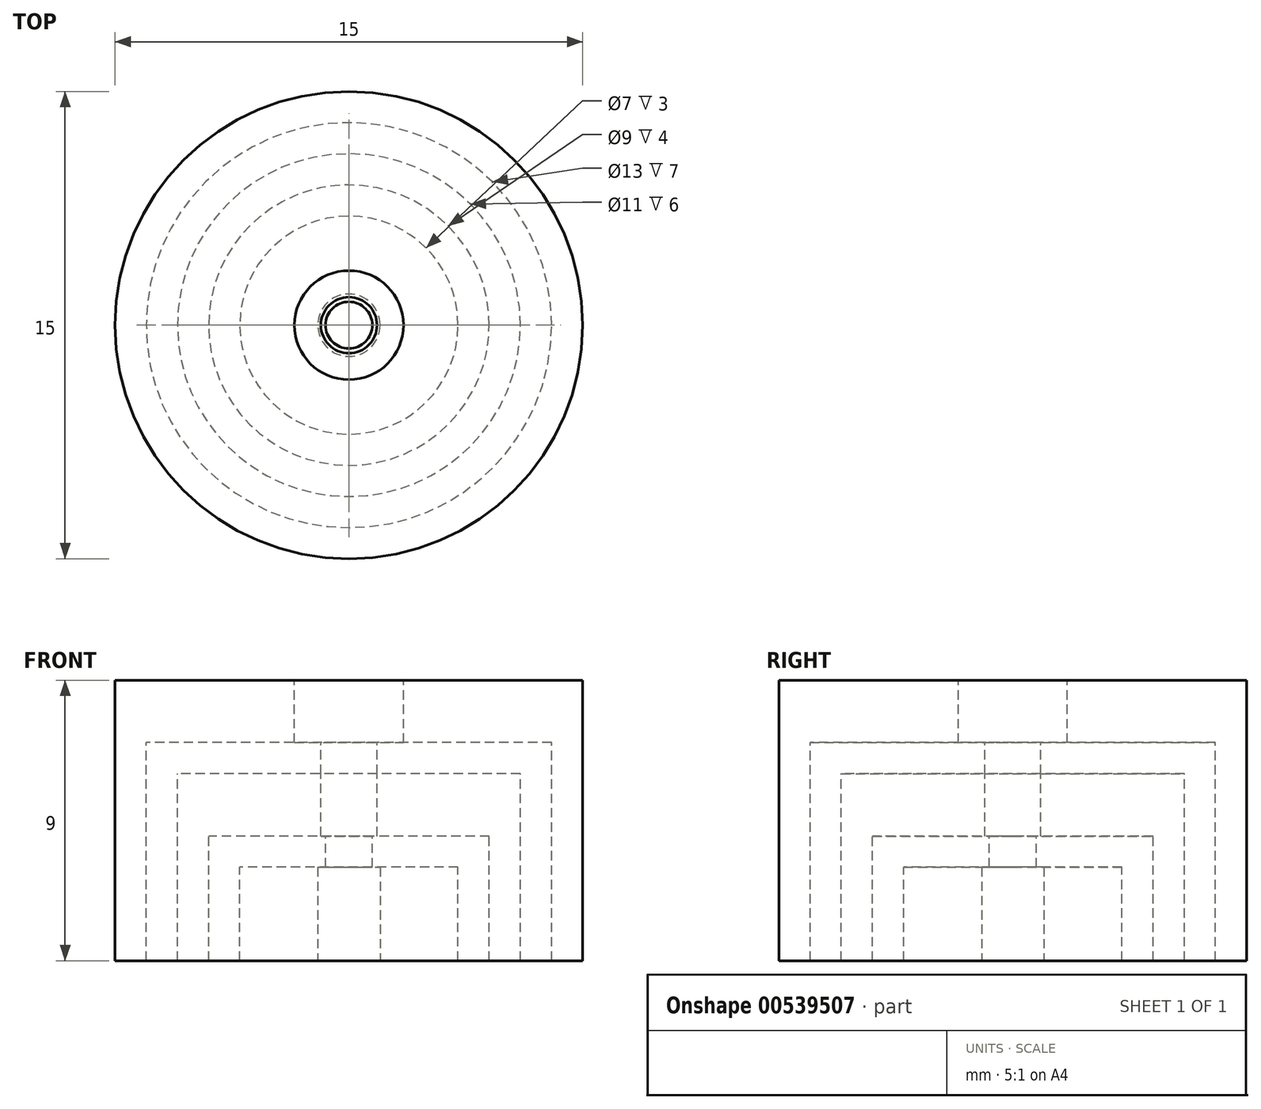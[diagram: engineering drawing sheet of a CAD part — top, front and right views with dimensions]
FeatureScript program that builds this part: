
annotation { "Feature Type Name" : "Feature", "Feature Type Description" : "" }
export const myFeature = defineFeature(function(context is Context, id is Id, definition is map)
    precondition{}
    {
        {
            var Q0;
            Q0=qCreatedBy(makeId("Front.planeOp"),FACE);
            var sketch = newSketch(context, id + "F0", { "sketchPlane" : qUnion([Q0])});
            skLineSegment(sketch, "E0", {"start": v(0, 0) * mm, "end": v(3.5, 0) * mm});
            skLineSegment(sketch, "E1", {"start": v(3.5, 0) * mm, "end": v(3.5, 3) * mm});
            skLineSegment(sketch, "E2", {"start": v(3.5, 3) * mm, "end": v(0, 3) * mm});
            skLineSegment(sketch, "E3", {"start": v(0, 3) * mm, "end": v(0, 0) * mm});
            skLineSegment(sketch, "E4", {"start": v(3.5, 0) * mm, "end": v(4.5, 0) * mm});
            skLineSegment(sketch, "E5", {"start": v(4.5, 0) * mm, "end": v(4.5, 4) * mm});
            skLineSegment(sketch, "E6", {"start": v(4.5, 4) * mm, "end": v(0, 4) * mm});
            skLineSegment(sketch, "E7", {"start": v(0, 5.5) * mm, "end": v(0, 0) * mm});
            skLineSegment(sketch, "E8", {"start": v(4.5, 0) * mm, "end": v(5.5, 0) * mm});
            skLineSegment(sketch, "E9", {"start": v(5.5, 0) * mm, "end": v(5.5, 6) * mm});
            skLineSegment(sketch, "E10", {"start": v(5.5, 6) * mm, "end": v(0, 6) * mm});
            skLineSegment(sketch, "E11", {"start": v(0, 9) * mm, "end": v(0, 0) * mm});
            skLineSegment(sketch, "E12", {"start": v(5.5, 0) * mm, "end": v(6.5, 0) * mm});
            skLineSegment(sketch, "E13", {"start": v(6.5, 0) * mm, "end": v(6.5, 7) * mm});
            skLineSegment(sketch, "E14", {"start": v(6.5, 7) * mm, "end": v(0, 7) * mm});
            skLineSegment(sketch, "E15", {"start": v(6.5, 0) * mm, "end": v(7.5, 0) * mm});
            skLineSegment(sketch, "E16", {"start": v(7.5, 0) * mm, "end": v(7.5, 9) * mm});
            skLineSegment(sketch, "E17", {"start": v(7.5, 9) * mm, "end": v(0, 9) * mm});
            skSolve(sketch);
        }
        {
            var Q0;
            Q0=makeQuery(id+"F0.imprint","IMPRINT",FACE,{"disambiguationData":[TD([[makeQuery(id+"F0.imprint","IMPRINT",EDGE,{"derivedFrom":sQuery(id+"F0.wireOp",EDGE,"E0")}),1.0]])]});
            var Q1;
            Q1=sQuery(id+"F0.wireOp",EDGE,"E3");
            revolve(context, id + "F1", {"entities" : qUnion([Q0]), "axis" : qUnion([Q1]), "revolveType" : RevolveType.FULL});
        }
        {
            var Q0;
            Q0=makeQuery(id+"F1.opRevolve","SWEPT_FACE",FACE,{"disambiguationData":[OSD([sQuery(id+"F0.wireOp",EDGE,"E0")])]});
            var sketch = newSketch(context, id + "F2", { "sketchPlane" : qUnion([Q0])});
            skCircle(sketch, "E18", {"center": v(0, 0) * mm, "radius": 1 * mm});
            skSolve(sketch);
        }
        {
            var Q0;
            Q0=makeQuery(id+"F2.imprint","IMPRINT",FACE,{"disambiguationData":[TD([[makeQuery(id+"F2.imprint","IMPRINT",EDGE,{"derivedFrom":sQuery(id+"F2.wireOp",EDGE,"E18")}),1.0]])]});
            var Q1;
            Q1=makeQuery(id+"F1.opRevolve","SWEPT_FACE",FACE,{"disambiguationData":[OSD([sQuery(id+"F0.wireOp",EDGE,"E2")])]});
            extrude(context, id + "F3", {"entities" : qUnion([Q0]), "operationType" : NewBodyOperationType.REMOVE, "endBound" : BoundingType.UP_TO_SURFACE, "oppositeDirection" : true, "depth" : 25 * mm, "endBoundEntityFace" : qUnion([Q1]), "offsetDistance" : 25 * mm});
        }
        {
            var Q0;
            Q0=makeQuery(id+"F0.imprint","IMPRINT",FACE,{"disambiguationData":[TD([[makeQuery(id+"F0.imprint","IMPRINT",EDGE,{"derivedFrom":sQuery(id+"F0.wireOp",EDGE,"E1")}),-1.0]])]});
            var Q1;
            Q1=sQuery(id+"F0.wireOp",EDGE,"E7");
            revolve(context, id + "F4", {"entities" : qUnion([Q0]), "axis" : qUnion([Q1]), "revolveType" : RevolveType.FULL});
        }
        {
            var Q0;
            Q0=makeQuery(id+"F4.opRevolve","SWEPT_FACE",FACE,{"disambiguationData":[OSD([sQuery(id+"F0.wireOp",EDGE,"E6")])]});
            var sketch = newSketch(context, id + "F5", { "sketchPlane" : qUnion([Q0])});
            skCircle(sketch, "E19", {"center": v(0, 0) * mm, "radius": 0.75 * mm});
            skSolve(sketch);
        }
        {
            var Q0;
            Q0=makeQuery(id+"F5.imprint","IMPRINT",FACE,{"disambiguationData":[TD([[makeQuery(id+"F5.imprint","IMPRINT",EDGE,{"derivedFrom":sQuery(id+"F5.wireOp",EDGE,"E19")}),1.0]])]});
            extrude(context, id + "F6", {"entities" : qUnion([Q0]), "operationType" : NewBodyOperationType.REMOVE, "endBound" : BoundingType.UP_TO_NEXT, "oppositeDirection" : true, "depth" : 25 * mm, "offsetDistance" : 25 * mm});
        }
        {
            var Q0;
            Q0=makeQuery(id+"F0.imprint","IMPRINT",FACE,{"disambiguationData":[TD([[makeQuery(id+"F0.imprint","IMPRINT",EDGE,{"derivedFrom":sQuery(id+"F0.wireOp",EDGE,"E5")}),-1.0]])]});
            var Q1;
            Q1=sQuery(id+"F0.wireOp",EDGE,"E11");
            revolve(context, id + "F7", {"entities" : qUnion([Q0]), "axis" : qUnion([Q1]), "revolveType" : RevolveType.FULL});
        }
        {
            var Q0;
            Q0=makeQuery(id+"F7.opRevolve","SWEPT_FACE",FACE,{"disambiguationData":[OSD([sQuery(id+"F0.wireOp",EDGE,"E10")])]});
            var sketch = newSketch(context, id + "F8", { "sketchPlane" : qUnion([Q0])});
            skCircle(sketch, "E20", {"center": v(0, 0) * mm, "radius": 0.9 * mm});
            skSolve(sketch);
        }
        {
            var Q0;
            Q0=makeQuery(id+"F8.imprint","IMPRINT",FACE,{"disambiguationData":[TD([[makeQuery(id+"F8.imprint","IMPRINT",EDGE,{"derivedFrom":sQuery(id+"F8.wireOp",EDGE,"E20")}),1.0]])]});
            extrude(context, id + "F9", {"entities" : qUnion([Q0]), "operationType" : NewBodyOperationType.REMOVE, "endBound" : BoundingType.UP_TO_NEXT, "oppositeDirection" : true, "depth" : 25 * mm, "offsetDistance" : 25 * mm});
        }
        {
            var Q0;
            Q0=makeQuery(id+"F0.imprint","IMPRINT",FACE,{"disambiguationData":[TD([[makeQuery(id+"F0.imprint","IMPRINT",EDGE,{"derivedFrom":sQuery(id+"F0.wireOp",EDGE,"E9")}),-1.0]])]});
            var Q1;
            Q1=sQuery(id+"F0.wireOp",EDGE,"E7");
            revolve(context, id + "F10", {"entities" : qUnion([Q0]), "axis" : qUnion([Q1]), "revolveType" : RevolveType.FULL});
        }
        {
            var Q0;
            Q0=makeQuery(id+"F10.opRevolve","SWEPT_FACE",FACE,{"disambiguationData":[OSD([sQuery(id+"F0.wireOp",EDGE,"E14")])]});
            var sketch = newSketch(context, id + "F11", { "sketchPlane" : qUnion([Q0])});
            skCircle(sketch, "E21", {"center": v(0, 0) * mm, "radius": 0.9 * mm});
            skSolve(sketch);
        }
        {
            var Q0;
            Q0=makeQuery(id+"F11.imprint","IMPRINT",FACE,{"disambiguationData":[TD([[makeQuery(id+"F11.imprint","IMPRINT",EDGE,{"derivedFrom":sQuery(id+"F11.wireOp",EDGE,"E21")}),1.0]])]});
            extrude(context, id + "F12", {"entities" : qUnion([Q0]), "operationType" : NewBodyOperationType.REMOVE, "endBound" : BoundingType.UP_TO_NEXT, "oppositeDirection" : true, "depth" : 25 * mm, "offsetDistance" : 25 * mm});
        }
        {
            var Q0;
            Q0=makeQuery(id+"F0.imprint","IMPRINT",FACE,{"disambiguationData":[TD([[makeQuery(id+"F0.imprint","IMPRINT",EDGE,{"derivedFrom":sQuery(id+"F0.wireOp",EDGE,"E13")}),-1.0]])]});
            var Q1;
            Q1=sQuery(id+"F0.wireOp",EDGE,"E7");
            revolve(context, id + "F13", {"entities" : qUnion([Q0]), "axis" : qUnion([Q1]), "revolveType" : RevolveType.FULL});
        }
        {
            var Q0;
            Q0=makeQuery(id+"F13.opRevolve","SWEPT_FACE",FACE,{"disambiguationData":[OSD([sQuery(id+"F0.wireOp",EDGE,"E17")])]});
            var sketch = newSketch(context, id + "F14", { "sketchPlane" : qUnion([Q0])});
            skCircle(sketch, "E22", {"center": v(0, 0) * mm, "radius": 1.75 * mm});
            skSolve(sketch);
        }
        {
            var Q0;
            Q0=makeQuery(id+"F14.imprint","IMPRINT",FACE,{"disambiguationData":[TD([[makeQuery(id+"F14.imprint","IMPRINT",EDGE,{"derivedFrom":sQuery(id+"F14.wireOp",EDGE,"E22")}),1.0]])]});
            extrude(context, id + "F15", {"entities" : qUnion([Q0]), "operationType" : NewBodyOperationType.REMOVE, "endBound" : BoundingType.UP_TO_NEXT, "oppositeDirection" : true, "depth" : 25 * mm, "offsetDistance" : 25 * mm});
        }
    });
